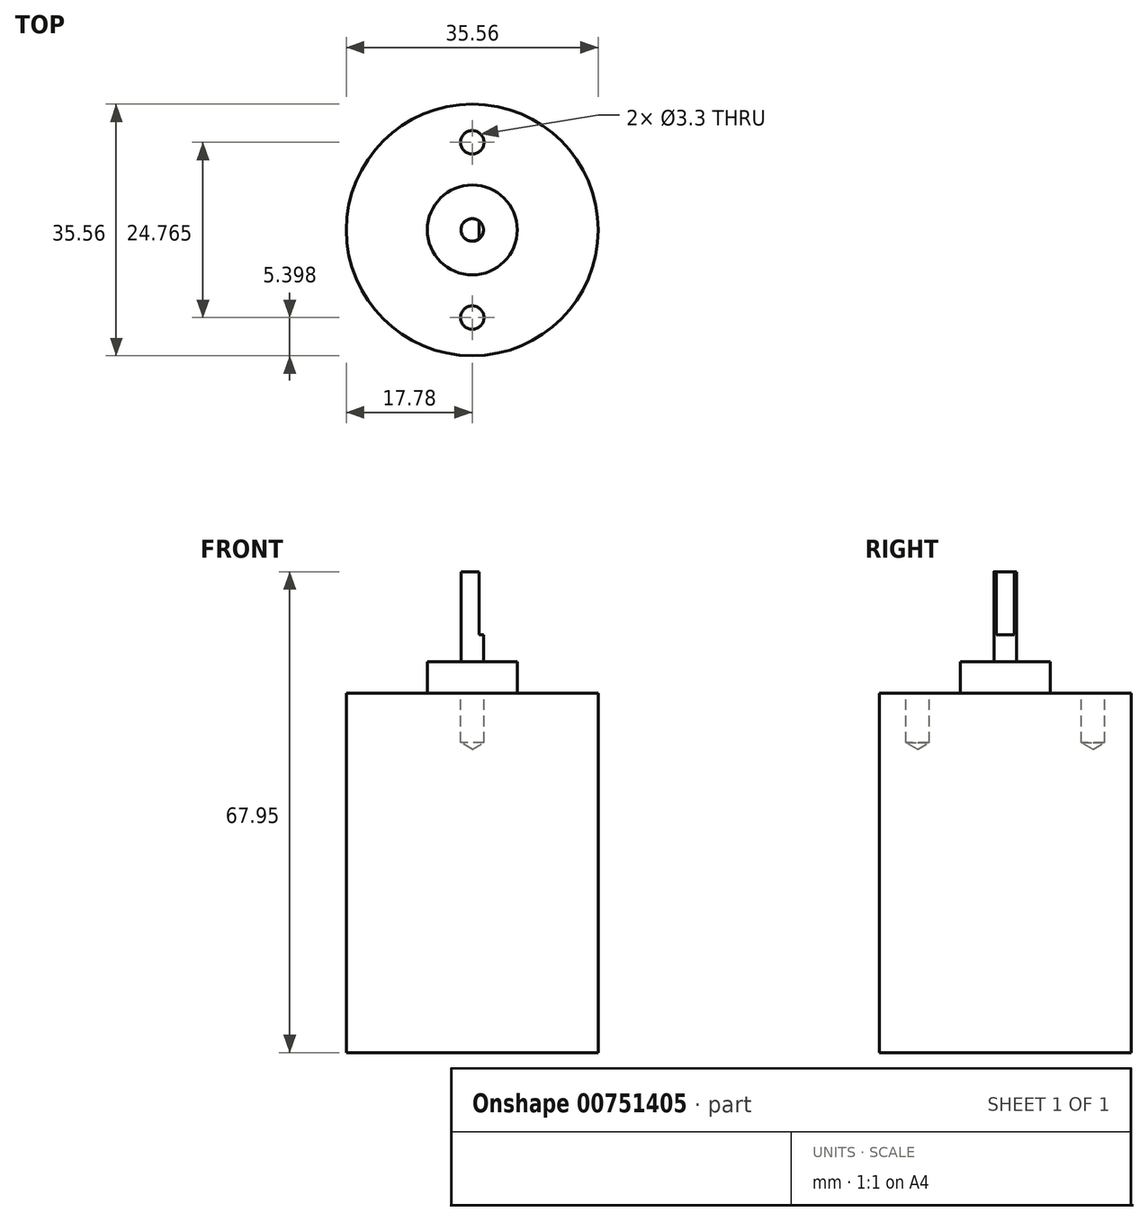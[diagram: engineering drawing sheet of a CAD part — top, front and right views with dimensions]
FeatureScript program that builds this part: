
annotation { "Feature Type Name" : "Feature", "Feature Type Description" : "" }
export const myFeature = defineFeature(function(context is Context, id is Id, definition is map)
    precondition{}
    {
        {
            var Q0;
            Q0=qCreatedBy(makeId("Top.planeOp"),FACE);
            var sketch = newSketch(context, id + "F0", { "sketchPlane" : qUnion([Q0])});
            skCircle(sketch, "E0", {"center": v(0, 0) * mm, "radius": 17.78 * mm});
            skCircle(sketch, "E1", {"center": v(0, 0) * mm, "radius": 6.35 * mm});
            skCircle(sketch, "E2", {"center": v(0, 0) * mm, "radius": 1.59 * mm});
            skLineSegment(sketch, "E3", {"start": v(0.95, 1.27) * mm, "end": v(0.95, -1.27) * mm});
            skSolve(sketch);
        }
        {
            var Q0;
            Q0=makeQuery(id+"F0.imprint","IMPRINT",FACE,{"disambiguationData":[TD([[makeQuery(id+"F0.imprint","IMPRINT",EDGE,{"derivedFrom":sQuery(id+"F0.wireOp",EDGE,"E0")}),1.0]])]});
            extrude(context, id + "F1", {"entities" : qUnion([Q0]), "depth" : 50.8 * mm, "offsetDistance" : 25.4 * mm});
        }
        {
            var Q0;
            Q0=makeQuery(id+"F0.imprint","IMPRINT",FACE,{"disambiguationData":[TD([[makeQuery(id+"F0.imprint","IMPRINT",EDGE,{"derivedFrom":sQuery(id+"F0.wireOp",EDGE,"E1")}),1.0]])]});
            extrude(context, id + "F2", {"entities" : qUnion([Q0]), "operationType" : NewBodyOperationType.ADD, "depth" : 55.24 * mm, "offsetDistance" : 25.4 * mm});
        }
        {
            var Q0;
            {var subQ0=sQuery(id+"F0.wireOp",EDGE,"E3");Q0=makeQuery(id+"F0.imprint","IMPRINT",FACE,{"disambiguationData":[TD([[makeQuery(id+"F0.imprint","IMPRINT",EDGE,{"derivedFrom":subQ0}),-1.0]])]});}
            extrude(context, id + "F3", {"entities" : qUnion([Q0]), "operationType" : NewBodyOperationType.ADD, "depth" : 67.94 * mm, "offsetDistance" : 25.4 * mm});
        }
        {
            var Q0;
            {var subQ0=sQuery(id+"F0.wireOp",EDGE,"E3");Q0=makeQuery(id+"F0.imprint","IMPRINT",FACE,{"disambiguationData":[TD([[makeQuery(id+"F0.imprint","IMPRINT",EDGE,{"derivedFrom":subQ0}),1.0]])]});}
            extrude(context, id + "F4", {"entities" : qUnion([Q0]), "operationType" : NewBodyOperationType.ADD, "depth" : 59.05 * mm, "offsetDistance" : 25.4 * mm});
        }
        {
            var Q0;
            Q0=makeQuery(id+"F1.opExtrude","CAP_FACE",FACE,{"disambiguationData":[OSD([sQuery(id+"F0.wireOp",EDGE,"E0"),sQuery(id+"F0.wireOp",EDGE,"E1")])],"isStart":false});
            var sketch = newSketch(context, id + "F5", { "sketchPlane" : qUnion([Q0])});
            skCircle(sketch, "E4", {"center": v(0, 0) * mm, "radius": 12.38 * mm, "construction": true});
            skPoint(sketch, "E5", {"position": v(0, 12.38) * mm});
            skPoint(sketch, "E6", {"position": v(0, -12.38) * mm});
            skSolve(sketch);
        }
        {
            var Q0;
            Q0=sQuery(id+"F5.wireOp",VERTEX,"E5");
            var Q1;
            Q1=sQuery(id+"F5.wireOp",VERTEX,"E6");
            var Q2;
            Q2=makeQuery(id+"F1.opExtrude","SWEPT_BODY",BODY,{"disambiguationData":[OSD([sQuery(id+"F0.wireOp",EDGE,"E0"),sQuery(id+"F0.wireOp",EDGE,"E1")])]});
            hole(context, id + "F6", {"style" : HoleStyle.SIMPLE, "endStyle" : HoleEndStyle.BLIND, "standardTappedOrClearance" : lookupTablePath({ "standard" : "ISO", "fit" : "Normal", "size" : "M3", "type" : "Clearance" }), "standardBlindInLast" : lookupTablePath({ "fit" : "Standard", "standard" : "ISO", "size" : "M3", "type" : "Clearance" }), "holeDiameter" : 3.3 * mm, "majorDiameter" : 6.35 * mm, "holeDepth" : 7 * mm, "isTappedThrough" : true, "tappedDepth" : 12.7 * mm, "tapClearance" : 3, "locations" : qUnion([Q0, Q1]), "scope" : qUnion([Q2])});
        }
    });
